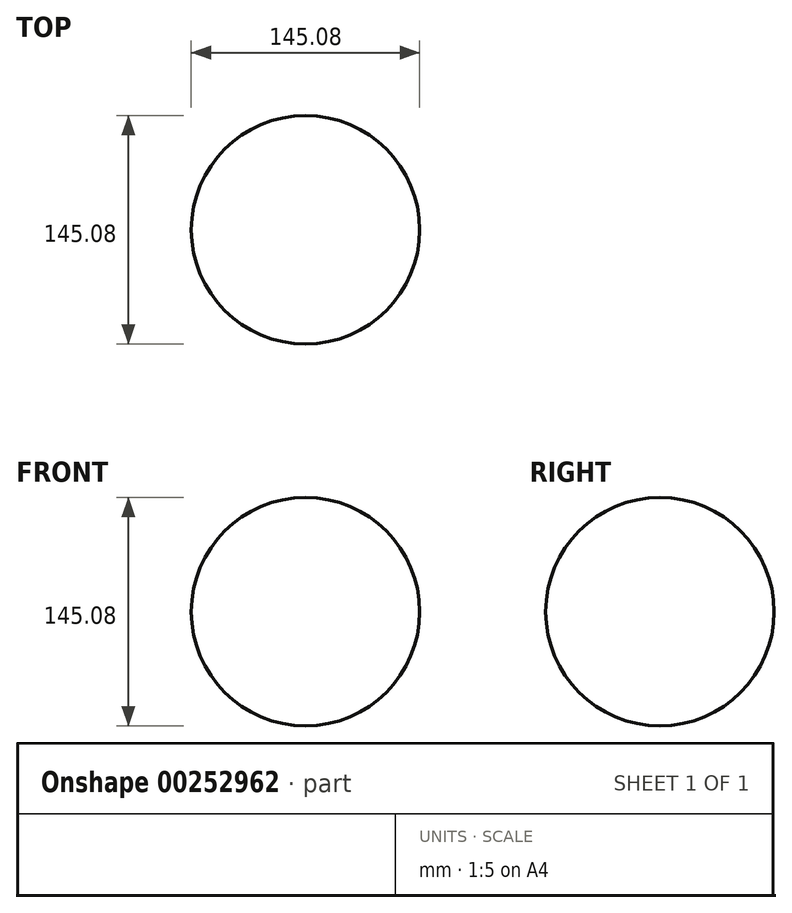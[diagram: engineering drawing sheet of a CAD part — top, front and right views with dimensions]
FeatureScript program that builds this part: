
annotation { "Feature Type Name" : "Feature", "Feature Type Description" : "" }
export const myFeature = defineFeature(function(context is Context, id is Id, definition is map)
    precondition{}
    {
        {
            var Q0;
            Q0=qCreatedBy(makeId("Front.planeOp"),FACE);
            var sketch = newSketch(context, id + "F0", { "sketchPlane" : qUnion([Q0])});
            skLineSegment(sketch, "E0", {"start": v(0, 84.2) * mm, "end": v(0, -103.89) * mm, "construction": true});
            skArc(sketch, "E1", {"start": v(0, -72.54) * mm, "mid": v(-72.54, 0) * mm, "end": v(0, 72.54) * mm});
            skSolve(sketch);
        }
        {
            var Q0;
            Q0 = qSketchRegion(id + "F0", true);
            var Q1;
            Q1=sQuery(id+"F0.wireOp",EDGE,"E1");
            var Q2;
            Q2=sQuery(id+"F0.wireOp",EDGE,"E0");
            revolve(context, id + "F1", {"bodyType" : ToolBodyType.SURFACE, "entities" : qUnion([Q0]), "surfaceEntities" : qUnion([Q1]), "axis" : qUnion([Q2]), "revolveType" : RevolveType.FULL});
        }
    });
